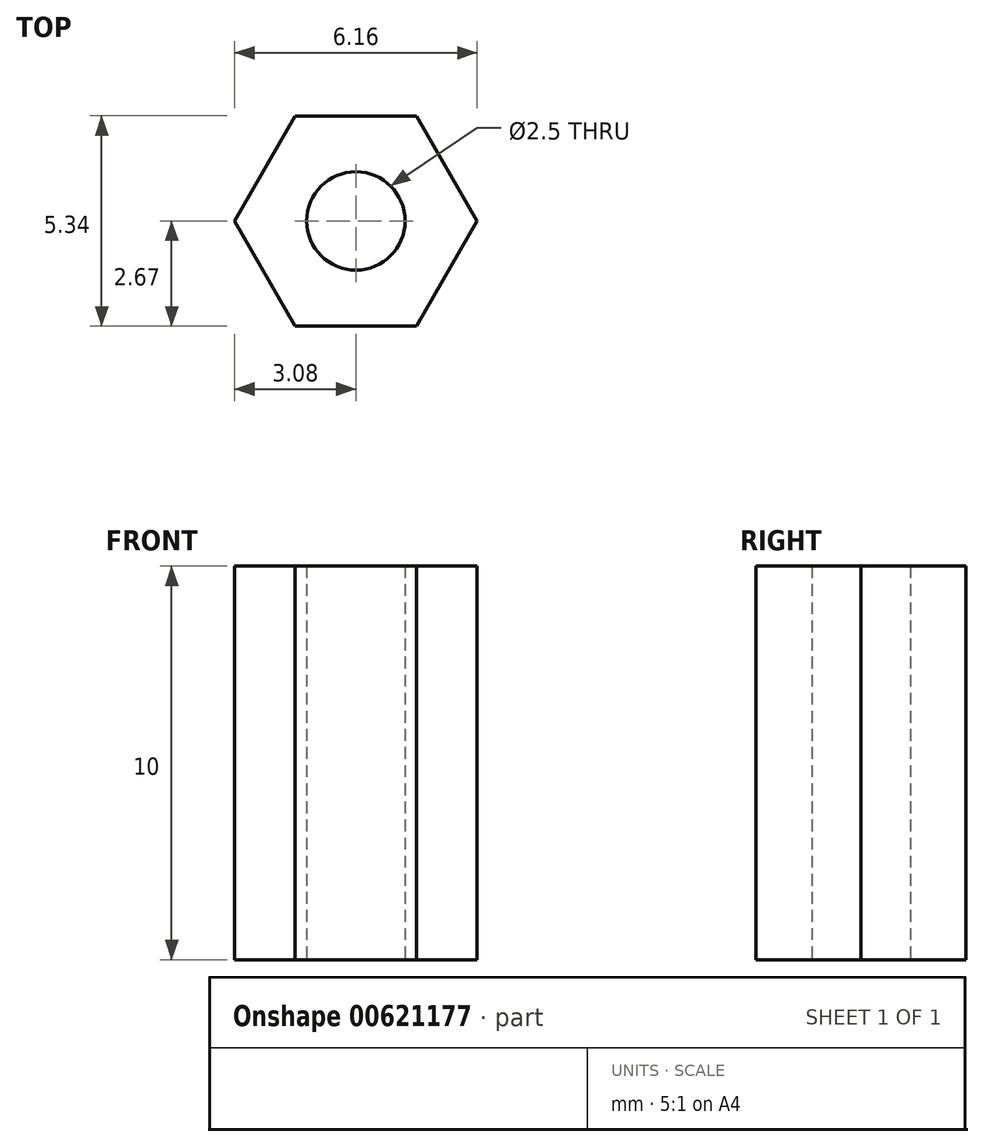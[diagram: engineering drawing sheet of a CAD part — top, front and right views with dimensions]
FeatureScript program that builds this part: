
annotation { "Feature Type Name" : "Feature", "Feature Type Description" : "" }
export const myFeature = defineFeature(function(context is Context, id is Id, definition is map)
    precondition{}
    {
        {
            var Q0;
            Q0=qCreatedBy(makeId("Top.planeOp"),FACE);
            var sketch = newSketch(context, id + "F0", { "sketchPlane" : qUnion([Q0])});
            skCircle(sketch, "E0.cCircle", {"center": v(0, 0) * mm, "radius": 2.67 * mm, "construction": true});
            skLineSegment(sketch, "E0.0", {"start": v(-1.54, 2.67) * mm, "end": v(1.54, 2.67) * mm});
            skLineSegment(sketch, "E0.1", {"start": v(1.54, 2.67) * mm, "end": v(3.08, 0) * mm});
            skLineSegment(sketch, "E0.2", {"start": v(3.08, 0) * mm, "end": v(1.54, -2.67) * mm});
            skLineSegment(sketch, "E0.3", {"start": v(1.54, -2.67) * mm, "end": v(-1.54, -2.67) * mm});
            skLineSegment(sketch, "E0.4", {"start": v(-1.54, -2.67) * mm, "end": v(-3.08, 0) * mm});
            skLineSegment(sketch, "E0.5", {"start": v(-3.08, 0) * mm, "end": v(-1.54, 2.67) * mm});
            skPoint(sketch, "E0.0.midPoint", {"position": v(0, 2.67) * mm});
            skSolve(sketch);
        }
        {
            var Q0;
            Q0=makeQuery(id+"F0.imprint","IMPRINT",FACE,{"disambiguationData":[TD([[makeQuery(id+"F0.imprint","IMPRINT",EDGE,{"derivedFrom":sQuery(id+"F0.wireOp",EDGE,"E0.0")}),-1.0]])]});
            extrude(context, id + "F1", {"entities" : qUnion([Q0]), "depth" : 10 * mm, "offsetDistance" : 25 * mm});
        }
        {
            var Q0;
            Q0=sQuery(id+"F0.wireOp",VERTEX,"E0.cCircle.center");
            var Q1;
            Q1=makeQuery(id+"F1.opExtrude","SWEPT_BODY",BODY,{"disambiguationData":[OSD([sQuery(id+"F0.wireOp",EDGE,"E0.0"),sQuery(id+"F0.wireOp",EDGE,"E0.1"),sQuery(id+"F0.wireOp",EDGE,"E0.2"),sQuery(id+"F0.wireOp",EDGE,"E0.3"),sQuery(id+"F0.wireOp",EDGE,"E0.4"),sQuery(id+"F0.wireOp",EDGE,"E0.5")])]});
            hole(context, id + "F2", {"style" : HoleStyle.SIMPLE, "endStyle" : HoleEndStyle.THROUGH, "oppositeDirection" : true, "standardTappedOrClearance" : lookupTablePath({ "standard" : "ISO", "engagement" : "75%", "pitch" : "0.5 mm", "size" : "M3", "type" : "Tapped" }), "standardBlindInLast" : lookupTablePath({ "standard" : "ISO", "engagement" : "75%", "pitch" : "0.5 mm", "size" : "M3", "type" : "Tapped" }), "holeDiameter" : 2.5 * mm, "majorDiameter" : 3 * mm, "showTappedDepth" : true, "isTappedThrough" : true, "tappedDepth" : 12 * mm, "tapClearance" : 3, "locations" : qUnion([Q0]), "scope" : qUnion([Q1])});
        }
    });
